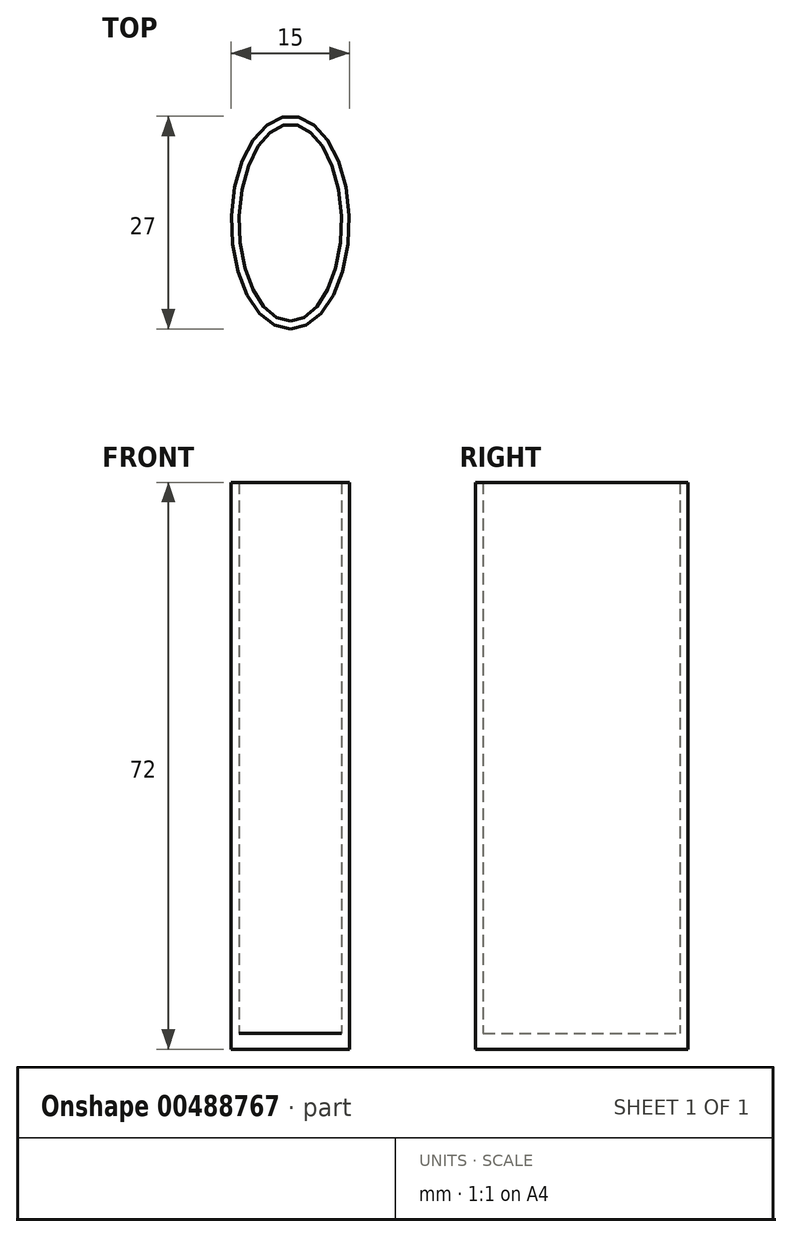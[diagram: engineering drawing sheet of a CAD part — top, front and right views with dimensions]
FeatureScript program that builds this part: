
annotation { "Feature Type Name" : "Feature", "Feature Type Description" : "" }
export const myFeature = defineFeature(function(context is Context, id is Id, definition is map)
    precondition{}
    {
        {
            var Q0;
            Q0=qCreatedBy(makeId("Top.planeOp"),FACE);
            var sketch = newSketch(context, id + "F0", { "sketchPlane" : qUnion([Q0])});
            skEllipse(sketch, "E0", {"center": v(0, 0) * mm, "majorRadius": 13.5 * mm, "minorRadius": 7.5 * mm, "majorAxis": v(0, -1)});
            skEllipse(sketch, "E1", {"center": v(0, 0) * mm, "majorRadius": 12.5 * mm, "minorRadius": 6.5 * mm, "majorAxis": v(0, -1)});
            skSolve(sketch);
        }
        {
            var Q0;
            Q0=makeQuery(id+"F0.imprint","IMPRINT",FACE,{"disambiguationData":[TD([[makeQuery(id+"F0.imprint","IMPRINT",EDGE,{"derivedFrom":sQuery(id+"F0.wireOp",EDGE,"E0")}),1.0]])]});
            extrude(context, id + "F1", {"entities" : qUnion([Q0]), "depth" : 70 * mm});
        }
        {
            var Q0;
            Q0=makeQuery(id+"F1.opExtrude","CAP_FACE",FACE,{"disambiguationData":[OSD([sQuery(id+"F0.wireOp",EDGE,"E0"),sQuery(id+"F0.wireOp",EDGE,"E1")])],"isStart":true});
            var sketch = newSketch(context, id + "F2", { "sketchPlane" : qUnion([Q0])});
            skEllipse(sketch, "E2", {"center": v(0, 0) * mm, "majorRadius": 13.5 * mm, "minorRadius": 7.5 * mm, "majorAxis": v(0, -1)});
            skSolve(sketch);
        }
        {
            var Q0;
            Q0 = qSketchRegion(id + "F2", true);
            extrude(context, id + "F3", {"entities" : qUnion([Q0]), "operationType" : NewBodyOperationType.ADD, "depth" : 2 * mm});
        }
    });
